FCSTD DOCUMENT  (FreeCAD 0.19R0.19.2)
Label: laptopStand007
License: All rights reserved
LicenseURL: http://en.wikipedia.org/wiki/All_rights_reserved
objects: Sketcher::SketchObject×1
note: 1 computed .brp shape members not serialized (recipe doc carries the construction recipe); baked Part::Feature solids carry a one-line shape summary decoded from their .brp

FEATURE [Sketcher::SketchObject] Sketch
  FullyConstrained = false
  sketch-geometry (105):
    g0: LineSegment StartX=-22.9272 StartY=136.221 StartZ=0 EndX=-22.9272 EndY=-103.779 EndZ=0
    g1: LineSegment StartX=-22.9272 StartY=136.221 StartZ=0 EndX=387.073 EndY=136.221 EndZ=0
    g2: LineSegment StartX=66.1121 StartY=95.2117 StartZ=0 EndX=66.1121 EndY=-84.7883 EndZ=0
    g3: LineSegment StartX=66.1121 StartY=95.2117 StartZ=0 EndX=256.112 EndY=95.2117 EndZ=0
    g4: LineSegment StartX=256.112 StartY=83.2117 StartZ=0 EndX=78.1121 EndY=83.2117 EndZ=0
    g5: LineSegment StartX=78.1121 StartY=-84.7883 StartZ=0 EndX=78.1121 EndY=83.2117 EndZ=0
    g6-g10: Circle x5 (B-spline internal-alignment scaffolding for g11; pole/knot coordinates omitted)
    g11: BSplineCurve PolesCount=5 KnotsCount=3 Degree=3 IsPeriodic=0
    g12: GeomPoint X=271.112 Y=85.2117 Z=0
    g13: GeomPoint X=258.112 Y=89.2117 Z=0
    g14: GeomPoint X=271.112 Y=89.2117 Z=0
    g15-g19: Circle x5 (B-spline internal-alignment scaffolding for g20; pole/knot coordinates omitted)
    g20: BSplineCurve PolesCount=5 KnotsCount=3 Degree=3 IsPeriodic=0
    g21: GeomPoint X=271.112 Y=93.2117 Z=0
    g22: GeomPoint X=284.112 Y=89.2117 Z=0
    g23: GeomPoint X=271.112 Y=89.2117 Z=0
    g24: LineSegment StartX=256.112 StartY=95.2117 StartZ=0 EndX=271.112 EndY=95.2117 EndZ=0
    g25: LineSegment StartX=271.112 StartY=93.2117 StartZ=0 EndX=271.112 EndY=95.2117 EndZ=0
    g26: LineSegment StartX=271.112 StartY=85.2117 StartZ=0 EndX=271.112 EndY=83.2117 EndZ=0
    g27: LineSegment StartX=271.112 StartY=83.2117 StartZ=0 EndX=256.112 EndY=83.2117 EndZ=0
    g28: LineSegment StartX=329.695 StartY=81.7679 StartZ=0 EndX=507.695 EndY=81.7679 EndZ=0
    g29: LineSegment StartX=329.695 StartY=93.7679 StartZ=0 EndX=519.695 EndY=93.7679 EndZ=0
    g30-g33: Circle x4 (B-spline internal-alignment scaffolding for g34; pole/knot coordinates omitted)
    g34: BSplineCurve PolesCount=5 KnotsCount=3 Degree=3 IsPeriodic=0
    g35: GeomPoint X=314.695 Y=83.7679 Z=0
    g36: GeomPoint X=301.695 Y=87.7679 Z=0
    g37: GeomPoint X=314.695 Y=87.7679 Z=0
    g38-g42: Circle x5 (B-spline internal-alignment scaffolding for g43; pole/knot coordinates omitted)
    g43: BSplineCurve PolesCount=5 KnotsCount=3 Degree=3 IsPeriodic=0
    g44: GeomPoint X=314.695 Y=91.7679 Z=0
    g45: GeomPoint X=327.695 Y=87.7679 Z=0
    g46: GeomPoint X=314.695 Y=87.7679 Z=0
    g47: LineSegment StartX=314.695 StartY=91.7679 StartZ=0 EndX=314.695 EndY=93.7679 EndZ=0
    g48: LineSegment StartX=329.695 StartY=81.7679 StartZ=0 EndX=314.695 EndY=81.7679 EndZ=0
    g49: LineSegment StartX=314.695 StartY=83.7679 StartZ=0 EndX=314.695 EndY=81.7679 EndZ=0
    g50: LineSegment StartX=329.695 StartY=93.7679 StartZ=0 EndX=314.695 EndY=93.7679 EndZ=0
    g51: LineSegment StartX=519.695 StartY=93.7679 StartZ=0 EndX=519.695 EndY=-86.2321 EndZ=0
    g52: LineSegment StartX=507.695 StartY=81.7679 StartZ=0 EndX=507.695 EndY=-86.2321 EndZ=0
    g53-g56: Circle x4 (B-spline internal-alignment scaffolding for g57; pole/knot coordinates omitted)
    g57: BSplineCurve PolesCount=5 KnotsCount=3 Degree=3 IsPeriodic=0
    g58: GeomPoint X=279.2 Y=54.9844 Z=0
    g59: GeomPoint X=266.2 Y=58.9844 Z=0
    g60: GeomPoint X=279.2 Y=58.9844 Z=0
    g61-g65: Circle x5 (B-spline internal-alignment scaffolding for g66; pole/knot coordinates omitted)
    g66: BSplineCurve PolesCount=5 KnotsCount=3 Degree=3 IsPeriodic=0
    g67: GeomPoint X=279.2 Y=62.9844 Z=0
    g68: GeomPoint X=292.2 Y=58.9844 Z=0
    g69: GeomPoint X=279.2 Y=58.9844 Z=0
    g70: LineSegment StartX=279.2 StartY=62.9844 StartZ=0 EndX=279.2 EndY=64.9844 EndZ=0
    g71: LineSegment StartX=279.2 StartY=54.9844 StartZ=0 EndX=279.2 EndY=52.9844 EndZ=0
    g72: LineSegment StartX=225.416 StartY=60.159 StartZ=0 EndX=237.416 EndY=60.159 EndZ=0
    g73: LineSegment StartX=237.416 StartY=60.159 StartZ=0 EndX=237.416 EndY=45.159 EndZ=0
    g74: LineSegment StartX=225.416 StartY=60.159 StartZ=0 EndX=225.416 EndY=45.159 EndZ=0
    g75: LineSegment StartX=225.416 StartY=45.159 StartZ=0 EndX=227.416 EndY=45.159 EndZ=0
    g76: LineSegment StartX=237.416 StartY=60.159 StartZ=0 EndX=237.416 EndY=56.159 EndZ=0
    g77: LineSegment StartX=225.416 StartY=60.159 StartZ=0 EndX=225.416 EndY=56.159 EndZ=0
    g78: LineSegment StartX=225.416 StartY=45.159 StartZ=0 EndX=225.416 EndY=30.159 EndZ=0
    g79: LineSegment StartX=237.416 StartY=45.159 StartZ=0 EndX=237.416 EndY=30.159 EndZ=0
    g80: LineSegment StartX=225.416 StartY=30.159 StartZ=0 EndX=237.416 EndY=30.159 EndZ=0
    g81: LineSegment StartX=237.416 StartY=60.159 StartZ=0 EndX=231.416 EndY=60.159 EndZ=0
    g82: LineSegment StartX=237.416 StartY=30.159 StartZ=0 EndX=237.416 EndY=34.159 EndZ=0
    g83: LineSegment StartX=225.416 StartY=30.159 StartZ=0 EndX=225.416 EndY=34.159 EndZ=0
    g84: LineSegment StartX=237.416 StartY=45.159 StartZ=0 EndX=235.416 EndY=45.159 EndZ=0
    g85: LineSegment StartX=235.416 StartY=45.159 StartZ=0 EndX=231.416 EndY=45.159 EndZ=0
    g86-g90: Circle x5 (B-spline internal-alignment scaffolding for g91; pole/knot coordinates omitted)
    g91: BSplineCurve PolesCount=5 KnotsCount=3 Degree=3 IsPeriodic=0
    g92: GeomPoint X=235.416 Y=45.159 Z=0
    g93: GeomPoint X=231.416 Y=58.159 Z=0
    g94: GeomPoint X=231.416 Y=45.159 Z=0
    g95: LineSegment StartX=225.416 StartY=30.159 StartZ=0 EndX=231.416 EndY=30.159 EndZ=0
    g96-g100: Circle x5 (B-spline internal-alignment scaffolding for g101; pole/knot coordinates omitted)
    g101: BSplineCurve PolesCount=5 KnotsCount=3 Degree=3 IsPeriodic=0
    g102: GeomPoint X=227.416 Y=45.159 Z=0
    g103: GeomPoint X=231.416 Y=32.159 Z=0
    g104: GeomPoint X=231.416 Y=45.159 Z=0
  constraints (168):
    c: Vertical(g0)
    c: Distance(g0) = 240
    c: Horizontal(g1)
    c: Distance(g1) = 410
    c: Coincident(g1,g0)
    c: Vertical(g2)
    c: Distance(g2) = 180
    c: Horizontal(g3)
    c: Distance(g3) = 190
    c: Coincident(g3,g2)
    c: Block(g2)
    c: Horizontal(g4)
    c: Vertical(g5)
    c: Coincident(g4,g5)
    c: Block(g4)
    c: Block(g5)
    c: Weight(g6) = 1
    c: Equal(g6, g7-g10) x4
    c: InternalAlignment(g6-g10 -> g11) x5
    c: InternalAlignment(g12,g11)
    c: InternalAlignment(g13,g11)
    c: InternalAlignment(g14,g11)
    c: Weight(g15) = 1
    c: Equal(g15, g16-g19) x4
    c: InternalAlignment(g15-g19 -> g20) x5
    c: InternalAlignment(g21,g20)
    c: InternalAlignment(g22,g20)
    c: InternalAlignment(g23,g20)
    c: Block(g20)
    c: Block(g11)
    c: Coincident(g24,g3)
    c: Horizontal(g24)
    c: Coincident(g25,g20)
    c: Vertical(g25)
    c: Coincident(g24,g25)
    c: Coincident(g26,g11)
    c: Vertical(g26)
    c: Coincident(g27,g4)
    c: Horizontal(g27)
    c: Block(g26)
    c: Block(g27)
    c: Horizontal(g28)
    c: Horizontal(g29)
    c: Block(g29)
    c: Equal(g30,g31)
    c: Equal(g30,g32)
    c: Equal(g30,g33)
    c: InternalAlignment(g30-g33 -> g34) x4
    c: InternalAlignment(g35,g34)
    c: InternalAlignment(g36,g34)
    c: InternalAlignment(g37,g34)
    c: Equal(g38, g39-g42) x4
    c: InternalAlignment(g38-g42 -> g43) x5
    c: InternalAlignment(g44,g43)
    c: InternalAlignment(g45,g43)
    c: InternalAlignment(g46,g43)
    c: Block(g43)
    c: Block(g34)
    c: Coincident(g47,g43)
    c: Vertical(g47)
    c: Block(g28)
    c: Coincident(g48,g28)
    c: Horizontal(g48)
    c: Coincident(g49,g34)
    c: Vertical(g49)
    c: Coincident(g49,g48)
    c: Coincident(g50,g29)
    c: Coincident(g50,g47)
    c: Horizontal(g50)
    c: Coincident(g51,g29)
    c: Vertical(g51)
    c: Distance(g51) = 180
    c: Coincident(g52,g28)
    c: Vertical(g52)
    c: Distance(g52) = 168
    c: Equal(g6,g53) = 1
    c: Equal(g53,g54)
    c: Equal(g53,g55)
    c: Equal(g53,g56)
    c: InternalAlignment(g53-g56 -> g57) x4
    c: InternalAlignment(g58,g57)
    c: InternalAlignment(g59,g57)
    c: InternalAlignment(g60,g57)
    c: Equal(g15,g61) = 1
    c: Equal(g61, g62-g65) x4
    c: InternalAlignment(g61-g65 -> g66) x5
    c: InternalAlignment(g67,g66)
    c: InternalAlignment(g68,g66)
    c: InternalAlignment(g69,g66)
    c: Block(g66)
    c: Block(g57)
    c: Coincident(g70,g66)
    c: Vertical(g70)
    c: Coincident(g71,g57)
    c: Vertical(g71)
    c: Block(g71)
    c: Horizontal(g72)
    c: Distance(g72) = 12
    c: Coincident(g73,g72)
    c: Vertical(g73)
    c: Distance(g73) = 15
    c: Coincident(g74,g72)
    c: Vertical(g74)
    c: Distance(g74) = 15
    c: Block(g72)
    c: Horizontal(g75)
    c: Distance(g75) = 2
    c: Coincident(g75,g74)
    c: Vertical(g76)
    c: Distance(g76) = 4
    c: Vertical(g77)
    c: Equal(g76,g77) = 4
    c: Coincident(g77,g72)
    c: Coincident(g76,g72)
    c: Coincident(g78,g74)
    c: Vertical(g78)
    c: Distance(g78) = 15
    c: Coincident(g79,g73)
    c: Vertical(g79)
    c: Coincident(g80,g78)
    c: Horizontal(g80)
    c: Coincident(g79,g80)
    c: Coincident(g81,g72)
    c: Horizontal(g81)
    c: Distance(g81) = 6
    c: Vertical(g82)
    c: Distance(g82) = 4
    c: Vertical(g83)
    c: Equal(g82,g83) = 4
    c: Coincident(g83,g78)
    c: Coincident(g82,g79)
    c: Coincident(g84,g73)
    c: Horizontal(g84)
    c: Distance(g84) = 2
    c: Coincident(g85,g84)
    c: Horizontal(g85)
    c: Distance(g85) = 4
    c: Coincident(g91,g84)
    c: Weight(g86) = 1
    c: Equal(g86,g87)
    c: Coincident(g87,g76)
    c: Equal(g86,g88)
    c: Coincident(g88,g81)
    c: Equal(g86,g89)
    c: Coincident(g89,g77)
    c: Equal(g86,g90)
    c: Coincident(g91,g85)
    c: InternalAlignment(g86-g90 -> g91) x5
    c: InternalAlignment(g92,g91)
    c: InternalAlignment(g93,g91)
    c: InternalAlignment(g94,g91)
    c: Horizontal(g95)
    c: Distance(g95) = 6
    c: Coincident(g95,g78)
    c: Coincident(g101,g75)
    c: Weight(g96) = 1
    c: Equal(g96,g97)
    c: Coincident(g97,g83)
    c: Equal(g96,g98)
    c: Coincident(g98,g95)
    c: Equal(g96,g99)
    c: Coincident(g99,g82)
    c: Equal(g96,g100)
    c: Coincident(g101,g85)
    c: InternalAlignment(g96-g100 -> g101) x5
    c: InternalAlignment(g102,g101)
    c: InternalAlignment(g103,g101)
    c: InternalAlignment(g104,g101)
